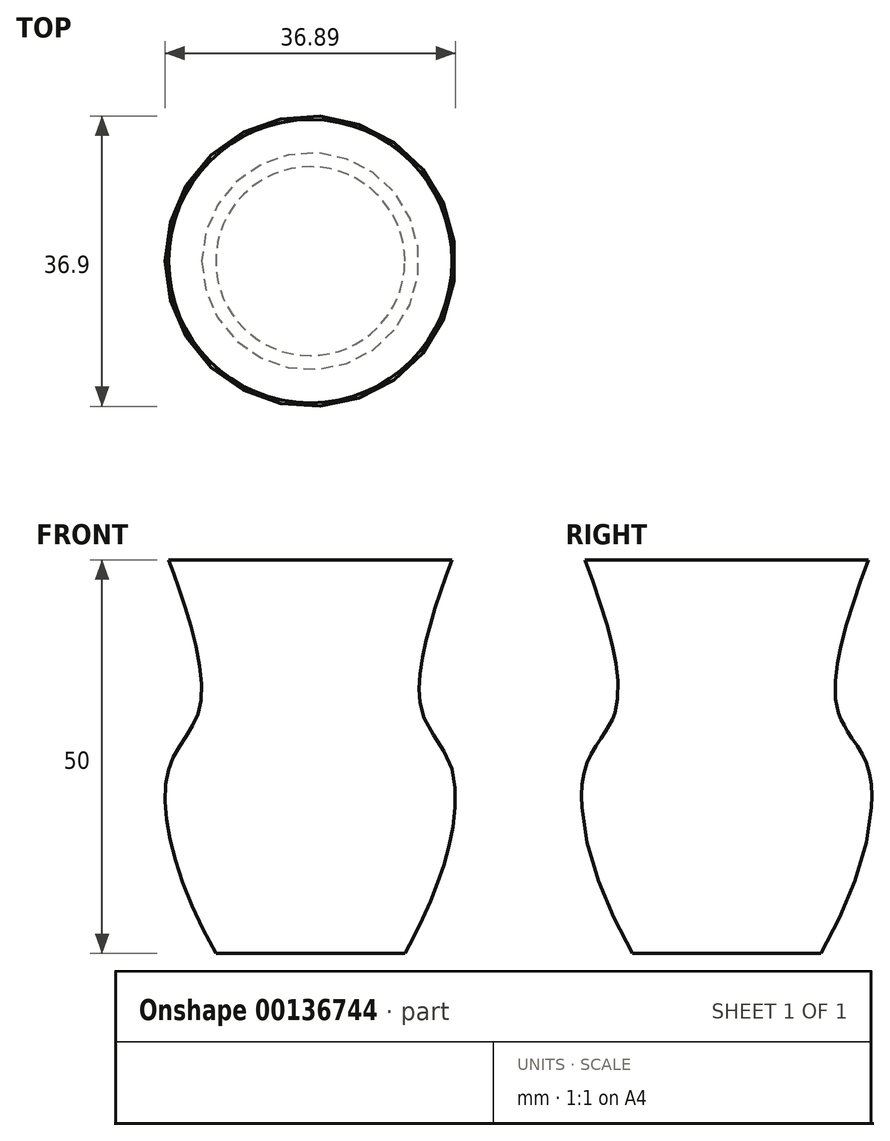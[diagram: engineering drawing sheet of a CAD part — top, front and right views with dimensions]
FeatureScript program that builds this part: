
annotation { "Feature Type Name" : "Feature", "Feature Type Description" : "" }
export const myFeature = defineFeature(function(context is Context, id is Id, definition is map)
    precondition{}
    {
        {
            var Q0;
            Q0=qCreatedBy(makeId("Front.planeOp"),FACE);
            var sketch = newSketch(context, id + "F0", { "sketchPlane" : qUnion([Q0])});
            skFitSpline(sketch, "E0", {"points": [v(18, 50) * mm, v(13.87, 32.1) * mm, v(17.89, 23.77) * mm, v(12, 0) * mm], "startDerivative": vector(-12.22, -33.02) * mm, "endDerivative": vector(-40.11, -70.96) * mm});
            skLineSegment(sketch, "E1", {"start": v(12, 0) * mm, "end": v(0, 0) * mm});
            skLineSegment(sketch, "E2", {"start": v(0, 0) * mm, "end": v(0, 50) * mm});
            skLineSegment(sketch, "E3", {"start": v(0, 50) * mm, "end": v(18, 50) * mm});
            skSolve(sketch);
        }
        {
            var Q0;
            Q0=makeQuery(id+"F0.imprint","IMPRINT",FACE,{"disambiguationData":[TD([[makeQuery(id+"F0.imprint","IMPRINT",EDGE,{"derivedFrom":sQuery(id+"F0.wireOp",EDGE,"E0")}),-1.0]])]});
            var Q1;
            Q1=sQuery(id+"F0.wireOp",EDGE,"E2");
            revolve(context, id + "F1", {"surfaceOperationType" : NewSurfaceOperationType.NEW, "entities" : qUnion([Q0]), "axis" : qUnion([Q1]), "revolveType" : RevolveType.FULL});
        }
    });
